# Revit family: Service_Sink-Wall_Hung-American_Standard-Clinic-9512999
name_source: partatom
category: Plumbing Fixtures
units: mm (PartAtom-declared; Revit-internal decimal feet)

## family parameters
Cut with Voids When Loaded = No
Host = Face
OmniClass Number = 23.45.05.14.14
OmniClass Title = Sinks/Lavatories
Part Type = Normal
Room Calculation Point = No
Round Connector Dimension = Use Diameter
Shared = Yes

## types (1)
- 9512999.020
    7832504.075**** Front stainless steel rim guard (1) = Yes
    7832512.075**** Side stainless steel rim guard (2) = Yes
    American Standard 6047117.002 or equivalent = No
    Assembly Code = D2010440
    Bedpan Diverter- American Standard 6047800.002 / 6047815.002 or equivalent = No
    CW Connection = Yes
    CWFU = 3
    Compliance Certifications = Fixture conforms to ANSI/ASME, A112.19.2M standards
    Default Elevation = 30"
    Description = Wall-Hung Clinic Service Sink
    Finish = Vitreous China-American Standard-020-White
    Flow Requirement = 25 gpm (96.6 L/min.)
    HW Connection = No
    HWFU = 3
    Height = 17 1/2"
    Installation Type = Wall Mounted
    Length = 25 1/4"
    Manufacturer = American Standard
    Material = Vitreous China-American Standard-020-White
    Model = 9512999.020
    NPT Connection Size = 1"
    Operating Pressure = 25 psi (flowing) - 80 psi (static)
    Product Documentation Link = https://americanstandard.box.com
    Product Page URL = https://www.americanstandard-us.com
    Revised Date = 10/13/2022
    Rim Material = Metal-American Standard-Steel
    Service Sink Faucet- American Standard 8345.115 or equivalent = No
    URL = http://www.americanstandard-us.com
    Vent Connection = No
    WFU = 4
    Waste Connection = Yes
    Waste Connection Diameter = 3"
    Width = 21 1/8"

## geometry (parser evidence)
native form markers: Sweep x2
no freeform markers — native parametric forms only
